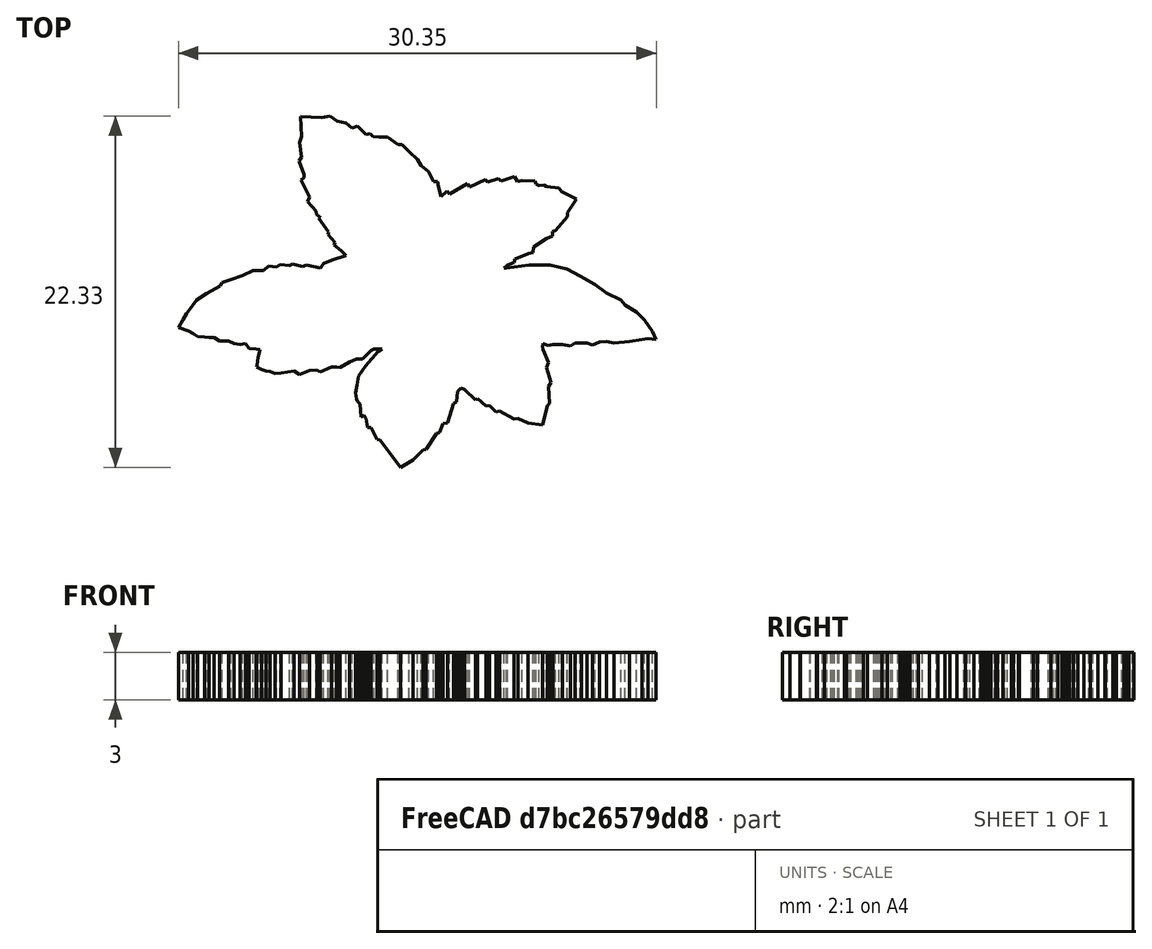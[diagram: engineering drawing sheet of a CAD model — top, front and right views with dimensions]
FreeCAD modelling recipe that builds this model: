
FCSTD DOCUMENT  (FreeCAD 0.20R29177 +233 (Git))
Label: mintsLeafLogo2022_10_12
License: All rights reserved
LicenseURL: http://en.wikipedia.org/wiki/All_rights_reserved
objects: Image::ImagePlane×1, Sketcher::SketchObject×1, PartDesign::Pad×1, PartDesign::Body×1
note: 4 computed .brp shape members not serialized (recipe doc carries the construction recipe); baked Part::Feature solids carry a one-line shape summary decoded from their .brp

FEATURE [Image::ImagePlane] ImagePlane
  XSize = 33.2103
  YSize = 25.9888
FEATURE [Sketcher::SketchObject] Sketch
  FullyConstrained = false
  MapMode = 5
  Support = -> [XY_Plane]
  sketch-geometry (205):
    g0: LineSegment StartX=-15.0667 StartY=-2.9879 StartZ=0 EndX=-14.4175 EndY=-3.20194 EndZ=0
    g1: LineSegment StartX=-14.1386 StartY=-3.3581 StartZ=0 EndX=-13.8673 EndY=-3.55064 EndZ=0
    g2: LineSegment StartX=-10.8098 StartY=-4.00788 StartZ=0 EndX=-10.5716 EndY=-4.29909 EndZ=0
    g3: LineSegment StartX=-10.5716 StartY=-4.29909 StartZ=0 EndX=-10.1338 EndY=-4.33136 EndZ=0
    g4: LineSegment StartX=-10.1338 StartY=-4.33136 StartZ=0 EndX=-9.89036 EndY=-4.3898 EndZ=0
    g5: LineSegment StartX=-9.51656 StartY=-5.73022 StartZ=0 EndX=-9.24931 EndY=-5.76229 EndZ=0
    g6: LineSegment StartX=-9.24931 StartY=-5.76229 StartZ=0 EndX=-8.92861 EndY=-5.90126 EndZ=0
    g7: LineSegment StartX=-8.92861 StartY=-5.90126 StartZ=0 EndX=-8.54378 EndY=-5.86384 EndZ=0
    g8: LineSegment StartX=-8.54378 StartY=-5.86384 StartZ=0 EndX=-7.71788 EndY=-5.75845 EndZ=0
    g9: LineSegment StartX=-7.71788 StartY=-5.75845 StartZ=0 EndX=-7.37291 EndY=-5.97257 EndZ=0
    g10: LineSegment StartX=-7.37291 StartY=-5.97257 StartZ=0 EndX=-6.72487 EndY=-5.72038 EndZ=0
    g11: LineSegment StartX=-6.72487 StartY=-5.72038 StartZ=0 EndX=-6.27066 EndY=-5.69481 EndZ=0
    g12: LineSegment StartX=-6.27066 StartY=-5.69481 StartZ=0 EndX=-6.06223 EndY=-5.80493 EndZ=0
    g13: LineSegment StartX=-6.06223 StartY=-5.80493 StartZ=0 EndX=-5.35089 EndY=-5.48914 EndZ=0
    g14: LineSegment StartX=-5.35089 StartY=-5.48914 StartZ=0 EndX=-5.02402 EndY=-5.48914 EndZ=0
    g15: LineSegment StartX=-5.02402 StartY=-5.48914 StartZ=0 EndX=-4.80126 EndY=-5.53132 EndZ=0
    g16: LineSegment StartX=-4.80126 StartY=-5.53132 StartZ=0 EndX=-4.19735 EndY=-5.16248 EndZ=0
    g17: LineSegment StartX=-3.75191 StartY=-4.97251 StartZ=0 EndX=-3.37714 EndY=-4.97251 EndZ=0
    g18: LineSegment StartX=-3.37714 StartY=-4.97251 StartZ=0 EndX=-2.81898 EndY=-4.45422 EndZ=0
    g19: LineSegment StartX=-2.81898 StartY=-4.45422 StartZ=0 EndX=-2.62761 EndY=-4.34259 EndZ=0
    g20: LineSegment StartX=-2.62761 StartY=-4.34259 StartZ=0 EndX=-2.15112 EndY=-4.35765 EndZ=0
    g21: LineSegment StartX=-2.38042 StartY=-4.51801 StartZ=0 EndX=-3.18577 EndY=-5.42702 EndZ=0
    g22: LineSegment StartX=-3.18577 StartY=-5.42702 StartZ=0 EndX=-3.61318 EndY=-6.05824 EndZ=0
    g23: LineSegment StartX=-3.61318 StartY=-6.05824 StartZ=0 EndX=-3.7111 EndY=-6.64579 EndZ=0
    g24: LineSegment StartX=-3.7111 StartY=-6.64579 StartZ=0 EndX=-3.83514 EndY=-7.15501 EndZ=0
    g25: LineSegment StartX=-3.83514 StartY=-7.15501 StartZ=0 EndX=-3.75878 EndY=-7.50876 EndZ=0
    g26: LineSegment StartX=-3.75878 StartY=-7.50876 StartZ=0 EndX=-3.70596 EndY=-7.68135 EndZ=0
    g27: LineSegment StartX=-3.70596 StartY=-7.68135 StartZ=0 EndX=-3.53967 EndY=-7.85202 EndZ=0
    g28: LineSegment StartX=-3.53967 StartY=-7.85202 StartZ=0 EndX=-3.4685 EndY=-8.65617 EndZ=0
    g29: LineSegment StartX=-3.27268 StartY=-8.56671 StartZ=0 EndX=-3.16823 EndY=-8.76909 EndZ=0
    g30: LineSegment StartX=-3.07088 StartY=-9.32083 StartZ=0 EndX=-2.84207 EndY=-9.3355 EndZ=0
    g31: LineSegment StartX=-2.84207 StartY=-9.3355 StartZ=0 EndX=-2.45193 EndY=-10.0982 EndZ=0
    g32: LineSegment StartX=-2.45193 StartY=-10.0982 StartZ=0 EndX=-2.24953 EndY=-10.1304 EndZ=0
    g33: LineSegment StartX=-2.24953 StartY=-10.1304 StartZ=0 EndX=-0.96042 EndY=-11.8753 EndZ=0
    g34: LineSegment StartX=-0.96042 StartY=-11.8753 StartZ=0 EndX=-0.153326 EndY=-11.3889 EndZ=0
    g35: LineSegment StartX=-0.153326 StartY=-11.3889 StartZ=0 EndX=0.461347 EndY=-10.7689 EndZ=0
    g36: LineSegment StartX=0.461347 StartY=-10.7689 StartZ=0 EndX=0.669802 EndY=-10.7261 EndZ=0
    g37: LineSegment StartX=0.669802 StartY=-10.7261 StartZ=0 EndX=1.31724 EndY=-9.70998 EndZ=0
    g38: LineSegment StartX=1.31724 StartY=-9.70998 StartZ=0 EndX=1.51826 EndY=-9.65081 EndZ=0
    g39: LineSegment StartX=1.51826 StartY=-9.65081 StartZ=0 EndX=1.74022 EndY=-9.08937 EndZ=0
    g40: LineSegment StartX=1.74022 StartY=-9.08937 StartZ=0 EndX=2.02094 EndY=-9.04367 EndZ=0
    g41: LineSegment StartX=2.02094 StartY=-9.04367 StartZ=0 EndX=2.39306 EndY=-7.80327 EndZ=0
    g42: LineSegment StartX=2.39306 StartY=-7.80327 StartZ=0 EndX=2.58839 EndY=-7.69871 EndZ=0
    g43: LineSegment StartX=2.6542 StartY=-7.03945 StartZ=0 EndX=2.86963 EndY=-6.81749 EndZ=0
    g44: LineSegment StartX=2.86963 StartY=-6.81749 StartZ=0 EndX=3.0916 EndY=-6.92847 EndZ=0
    g45: LineSegment StartX=3.0916 StartY=-6.92847 StartZ=0 EndX=3.79666 EndY=-7.57478 EndZ=0
    g46: LineSegment StartX=3.79666 StartY=-7.57478 StartZ=0 EndX=3.93376 EndY=-7.50297 EndZ=0
    g47: LineSegment StartX=3.93376 StartY=-7.50297 StartZ=0 EndX=4.46256 EndY=-7.97301 EndZ=0
    g48: LineSegment StartX=4.46256 StartY=-7.97301 StartZ=0 EndX=4.68452 EndY=-7.92079 EndZ=0
    g49: LineSegment StartX=4.68452 StartY=-7.92079 StartZ=0 EndX=5.1154 EndY=-8.34513 EndZ=0
    g50: LineSegment StartX=5.1154 StartY=-8.34513 StartZ=0 EndX=5.32431 EndY=-8.28637 EndZ=0
    g51: LineSegment StartX=5.32431 StartY=-8.28637 StartZ=0 EndX=6.23668 EndY=-8.79564 EndZ=0
    g52: LineSegment StartX=6.23668 StartY=-8.79564 StartZ=0 EndX=6.50362 EndY=-8.76631 EndZ=0
    g53: LineSegment StartX=6.50362 StartY=-8.76631 StartZ=0 EndX=7.14802 EndY=-9.05537 EndZ=0
    g54: LineSegment StartX=7.14802 StartY=-9.05537 StartZ=0 EndX=8.04883 EndY=-9.18613 EndZ=0
    g55: LineSegment StartX=8.04883 StartY=-9.18613 StartZ=0 EndX=8.36847 EndY=-7.93662 EndZ=0
    g56: LineSegment StartX=8.36847 StartY=-7.93662 StartZ=0 EndX=8.49923 EndY=-7.79133 EndZ=0
    g57: LineSegment StartX=8.49923 StartY=-7.79133 StartZ=0 EndX=8.43477 EndY=-6.72206 EndZ=0
    g58: LineSegment StartX=8.43477 StartY=-6.72206 StartZ=0 EndX=8.58621 EndY=-6.47988 EndZ=0
    g59: LineSegment StartX=8.58621 StartY=-6.47988 StartZ=0 EndX=8.32296 EndY=-5.53178 EndZ=0
    g60: LineSegment StartX=8.32296 StartY=-5.53178 StartZ=0 EndX=8.43984 EndY=-5.19091 EndZ=0
    g61: LineSegment StartX=8.43984 StartY=-5.19091 StartZ=0 EndX=8.07426 EndY=-4.39307 EndZ=0
    g62: LineSegment StartX=8.07426 StartY=-4.39307 StartZ=0 EndX=8.04236 EndY=-4.17777 EndZ=0
    g63: LineSegment StartX=8.04236 StartY=-4.17777 StartZ=0 EndX=8.0902 EndY=-3.99438 EndZ=0
    g64: LineSegment StartX=8.4103 StartY=-4.11103 StartZ=0 EndX=8.72013 EndY=-4.0502 EndZ=0
    g65: LineSegment StartX=8.72013 StartY=-4.0502 StartZ=0 EndX=9.31817 EndY=-4.0502 EndZ=0
    g66: LineSegment StartX=9.31817 StartY=-4.0502 StartZ=0 EndX=9.82964 EndY=-4.15887 EndZ=0
    g67: LineSegment StartX=10.1326 StartY=-3.9675 StartZ=0 EndX=10.5175 EndY=-3.9623 EndZ=0
    g68: LineSegment StartX=10.5175 StartY=-3.9623 StartZ=0 EndX=10.8831 EndY=-3.97536 EndZ=0
    g69: LineSegment StartX=10.8831 StartY=-3.97536 StartZ=0 EndX=11.2245 EndY=-4.09431 EndZ=0
    g70: LineSegment StartX=11.2245 StartY=-4.09431 StartZ=0 EndX=11.6861 EndY=-3.91007 EndZ=0
    g71: LineSegment StartX=11.6861 StartY=-3.91007 StartZ=0 EndX=12.1039 EndY=-3.88396 EndZ=0
    g72: LineSegment StartX=12.1039 StartY=-3.88396 StartZ=0 EndX=12.6 EndY=-3.9623 EndZ=0
    g73: LineSegment StartX=12.6 StartY=-3.9623 StartZ=0 EndX=13.5793 EndY=-3.87743 EndZ=0
    g74: LineSegment StartX=13.5793 StartY=-3.87743 StartZ=0 EndX=14.3888 EndY=-3.74687 EndZ=0
    g75: LineSegment StartX=14.3888 StartY=-3.74687 StartZ=0 EndX=14.7544 EndY=-3.68158 EndZ=0
    g76: LineSegment StartX=14.7544 StartY=-3.68158 StartZ=0 EndX=15.2767 EndY=-3.75339 EndZ=0
    g77: LineSegment StartX=15.2767 StartY=-3.75339 StartZ=0 EndX=15.0432 EndY=-3.24137 EndZ=0
    g78: LineSegment StartX=15.0432 StartY=-3.24137 StartZ=0 EndX=14.5209 EndY=-2.51672 EndZ=0
    g79: LineSegment StartX=14.5209 StartY=-2.51672 StartZ=0 EndX=14.0378 EndY=-1.99445 EndZ=0
    g80: LineSegment StartX=14.0378 StartY=-1.99445 StartZ=0 EndX=13.2802 EndY=-1.54625 EndZ=0
    g81: LineSegment StartX=13.2802 StartY=-1.54625 StartZ=0 EndX=13.0438 EndY=-1.23117 EndZ=0
    g82: LineSegment StartX=13.0438 StartY=-1.23117 StartZ=0 EndX=12.1074 EndY=-0.797939 EndZ=0
    g83: LineSegment StartX=12.1074 StartY=-0.797939 StartZ=0 EndX=11.3804 EndY=-0.250878 EndZ=0
    g84: LineSegment StartX=11.3804 StartY=-0.250878 StartZ=0 EndX=10.4396 EndY=0.304889 EndZ=0
    g85: LineSegment StartX=10.4396 StartY=0.304889 StartZ=0 EndX=9.59526 EndY=0.727998 EndZ=0
    g86: LineSegment StartX=9.59526 StartY=0.727998 StartZ=0 EndX=8.53624 EndY=0.97306 EndZ=0
    g87: LineSegment StartX=8.53624 StartY=0.97306 StartZ=0 EndX=7.199 EndY=0.97306 EndZ=0
    g88: LineSegment StartX=7.199 StartY=0.97306 StartZ=0 EndX=5.77932 EndY=0.795578 EndZ=0
    g89: LineSegment StartX=5.77932 StartY=0.795578 StartZ=0 EndX=5.60186 EndY=0.795578 EndZ=0
    g90: LineSegment StartX=5.60186 StartY=0.795578 StartZ=0 EndX=5.83178 EndY=0.981815 EndZ=0
    g91: LineSegment StartX=5.83178 StartY=0.981815 StartZ=0 EndX=6.25403 EndY=1.1582 EndZ=0
    g92: LineSegment StartX=6.30214 StartY=1.38269 StartZ=0 EndX=7.17987 EndY=1.70686 EndZ=0
    g93: LineSegment StartX=7.17987 StartY=1.70686 StartZ=0 EndX=7.44682 EndY=1.79438 EndZ=0
    g94: LineSegment StartX=7.44682 StartY=1.79438 StartZ=0 EndX=7.49058 EndY=2.12696 EndZ=0
    g95: LineSegment StartX=7.49058 StartY=2.12696 StartZ=0 EndX=8.30058 EndY=2.66839 EndZ=0
    g96: LineSegment StartX=8.30058 StartY=2.66839 StartZ=0 EndX=8.68575 EndY=2.81854 EndZ=0
    g97: LineSegment StartX=8.68575 StartY=2.81854 StartZ=0 EndX=8.68575 EndY=3.12537 EndZ=0
    g98: LineSegment StartX=8.68575 StartY=3.12537 StartZ=0 EndX=8.89508 EndY=3.18684 EndZ=0
    g99: LineSegment StartX=8.89508 StartY=3.18684 StartZ=0 EndX=9.63492 EndY=4.06602 EndZ=0
    g100: LineSegment StartX=9.63492 StartY=4.06602 StartZ=0 EndX=9.62638 EndY=4.32743 EndZ=0
    g101: LineSegment StartX=9.62638 StartY=4.32743 StartZ=0 EndX=10.2068 EndY=5.18314 EndZ=0
    g102: LineSegment StartX=10.2068 StartY=5.18314 StartZ=0 EndX=9.25518 EndY=5.64445 EndZ=0
    g103: LineSegment StartX=9.1102 StartY=5.87597 StartZ=0 EndX=8.32132 EndY=5.97336 EndZ=0
    g104: LineSegment StartX=8.32132 StartY=5.97336 StartZ=0 EndX=8.15466 EndY=6.06625 EndZ=0
    g105: LineSegment StartX=7.63471 StartY=6.13088 StartZ=0 EndX=7.56391 EndY=6.33267 EndZ=0
    g106: LineSegment StartX=7.56391 StartY=6.33267 StartZ=0 EndX=6.74832 EndY=6.35496 EndZ=0
    g107: LineSegment StartX=6.74832 StartY=6.35496 StartZ=0 EndX=6.46819 EndY=6.29526 EndZ=0
    g108: LineSegment StartX=6.46819 StartY=6.29526 StartZ=0 EndX=6.27042 EndY=6.61061 EndZ=0
    g109: LineSegment StartX=6.27042 StartY=6.61061 StartZ=0 EndX=5.40453 EndY=6.33267 EndZ=0
    g110: LineSegment StartX=5.40453 StartY=6.33267 StartZ=0 EndX=5.27091 EndY=6.47164 EndZ=0
    g111: LineSegment StartX=5.27091 StartY=6.47164 StartZ=0 EndX=4.56942 EndY=6.24725 EndZ=0
    g112: LineSegment StartX=4.56942 StartY=6.24725 StartZ=0 EndX=4.44161 EndY=6.40652 EndZ=0
    g113: LineSegment StartX=4.44161 StartY=6.40652 StartZ=0 EndX=3.4195 EndY=5.94588 EndZ=0
    g114: LineSegment StartX=3.4195 StartY=5.94588 StartZ=0 EndX=3.29192 EndY=6.1532 EndZ=0
    g115: LineSegment StartX=3.29192 StartY=6.1532 StartZ=0 EndX=2.15964 EndY=5.49137 EndZ=0
    g116: LineSegment StartX=2.15964 StartY=5.49137 StartZ=0 EndX=2.00016 EndY=5.69869 EndZ=0
    g117: LineSegment StartX=2.00016 StartY=5.69869 StartZ=0 EndX=1.6185 EndY=5.34828 EndZ=0
    g118: LineSegment StartX=1.6185 StartY=5.34828 StartZ=0 EndX=1.45984 EndY=5.94974 EndZ=0
    g119: LineSegment StartX=1.38165 StartY=6.28651 StartZ=0 EndX=1.14534 EndY=6.29963 EndZ=0
    g120: LineSegment StartX=0.348522 StartY=7.29544 StartZ=0 EndX=0.126706 EndY=7.68126 EndZ=0
    g121: LineSegment StartX=0.126706 StartY=7.68126 StartZ=0 EndX=-0.415308 EndY=8.18163 EndZ=0
    g122: LineSegment StartX=-0.415308 StartY=8.18163 StartZ=0 EndX=-0.872658 EndY=8.6237 EndZ=0
    g123: LineSegment StartX=-0.872658 StartY=8.6237 StartZ=0 EndX=-1.12074 EndY=8.64329 EndZ=0
    g124: LineSegment StartX=-1.12074 StartY=8.64329 StartZ=0 EndX=-1.79316 EndY=9.11986 EndZ=0
    g125: LineSegment StartX=-1.79316 StartY=9.11986 StartZ=0 EndX=-2.31488 EndY=9.12122 EndZ=0
    g126: LineSegment StartX=-2.31488 StartY=9.12122 StartZ=0 EndX=-2.71321 EndY=9.13846 EndZ=0
    g127: LineSegment StartX=-2.71321 StartY=9.13846 StartZ=0 EndX=-2.88425 EndY=9.34157 EndZ=0
    g128: LineSegment StartX=-2.88425 StartY=9.34157 StartZ=0 EndX=-3.16779 EndY=9.26454 EndZ=0
    g129: LineSegment StartX=-3.70739 StartY=9.82796 StartZ=0 EndX=-4.04915 EndY=9.7003 EndZ=0
    g130: LineSegment StartX=-4.04915 StartY=9.7003 StartZ=0 EndX=-4.42988 EndY=10.011 EndZ=0
    g131: LineSegment StartX=-5.98947 StartY=10.3656 StartZ=0 EndX=-7.32605 EndY=10.4108 EndZ=0
    g132: LineSegment StartX=-7.25254 StartY=9.13254 StartZ=0 EndX=-7.36878 EndY=8.7693 EndZ=0
    g133: LineSegment StartX=-7.36878 StartY=8.7693 StartZ=0 EndX=-7.2614 EndY=7.83762 EndZ=0
    g134: LineSegment StartX=-7.2614 StartY=7.83762 StartZ=0 EndX=-7.41112 EndY=7.6042 EndZ=0
    g135: LineSegment StartX=-7.41112 StartY=7.6042 StartZ=0 EndX=-7.09216 EndY=6.74302 EndZ=0
    g136: LineSegment StartX=-7.09216 StartY=6.74302 StartZ=0 EndX=-7.10014 EndY=6.55962 EndZ=0
    g137: LineSegment StartX=-7.10014 StartY=6.55962 StartZ=0 EndX=-7.29151 EndY=6.3842 EndZ=0
    g138: LineSegment StartX=-7.29151 StartY=6.3842 StartZ=0 EndX=-6.74132 EndY=5.29976 EndZ=0
    g139: LineSegment StartX=-6.74132 StartY=5.29976 StartZ=0 EndX=-6.87495 EndY=5.02732 EndZ=0
    g140: LineSegment StartX=-6.87495 StartY=5.02732 StartZ=0 EndX=-6.31586 EndY=4.42065 EndZ=0
    g141: LineSegment StartX=-6.31586 StartY=4.42065 StartZ=0 EndX=-6.30396 EndY=4.19463 EndZ=0
    g142: LineSegment StartX=-6.30396 StartY=4.19463 StartZ=0 EndX=-6.05415 EndY=4.0043 EndZ=0
    g143: LineSegment StartX=-6.05415 StartY=4.0043 StartZ=0 EndX=-6.18501 EndY=3.95672 EndZ=0
    g144: LineSegment StartX=-6.18501 StartY=3.95672 StartZ=0 EndX=-5.54265 EndY=3.07645 EndZ=0
    g145: LineSegment StartX=-5.54265 StartY=3.07645 StartZ=0 EndX=-5.57833 EndY=2.90991 EndZ=0
    g146: LineSegment StartX=-5.57833 StartY=2.90991 StartZ=0 EndX=-5.1263 EndY=2.41029 EndZ=0
    g147: LineSegment StartX=-5.1263 StartY=2.41029 StartZ=0 EndX=-5.18578 EndY=2.26755 EndZ=0
    g148: LineSegment StartX=-5.18578 StartY=2.26755 StartZ=0 EndX=-4.73375 EndY=1.89878 EndZ=0
    g149: LineSegment StartX=-4.73375 StartY=1.89878 StartZ=0 EndX=-4.42446 EndY=1.5895 EndZ=0
    g150: LineSegment StartX=-4.42446 StartY=1.5895 StartZ=0 EndX=-5.31663 EndY=1.29211 EndZ=0
    g151: LineSegment StartX=-5.31663 StartY=1.29211 StartZ=0 EndX=-5.84004 EndY=1.08988 EndZ=0
    g152: LineSegment StartX=-5.84004 StartY=1.08988 StartZ=0 EndX=-6.04226 EndY=0.792495 EndZ=0
    g153: LineSegment StartX=-6.04226 StartY=0.792495 StartZ=0 EndX=-6.94632 EndY=0.994719 EndZ=0
    g154: LineSegment StartX=-6.94632 StartY=0.994719 StartZ=0 EndX=-7.19613 EndY=0.887659 EndZ=0
    g155: LineSegment StartX=-7.19613 StartY=0.887659 StartZ=0 EndX=-7.8147 EndY=1.0423 EndZ=0
    g156: LineSegment StartX=-7.8147 StartY=1.0423 StartZ=0 EndX=-8.02502 EndY=0.969153 EndZ=0
    g157: LineSegment StartX=-8.02502 StartY=0.969153 StartZ=0 EndX=-8.60267 EndY=1.03042 EndZ=0
    g158: LineSegment StartX=-8.60267 StartY=1.03042 StartZ=0 EndX=-8.8346 EndY=0.872878 EndZ=0
    g159: LineSegment StartX=-8.8346 StartY=0.872878 StartZ=0 EndX=-9.33349 EndY=0.929767 EndZ=0
    g160: LineSegment StartX=-9.33349 StartY=0.929767 StartZ=0 EndX=-9.66169 EndY=0.649695 EndZ=0
    g161: LineSegment StartX=-9.66169 StartY=0.649695 StartZ=0 EndX=-10.3249 EndY=0.649695 EndZ=0
    g162: LineSegment StartX=-10.3249 StartY=0.649695 StartZ=0 EndX=-11.0107 EndY=0.32425 EndZ=0
    g163: LineSegment StartX=-11.0107 StartY=0.32425 StartZ=0 EndX=-11.7283 EndY=0.053139 EndZ=0
    g164: LineSegment StartX=-11.7283 StartY=0.053139 StartZ=0 EndX=-12.2971 EndY=-0.13161 EndZ=0
    g165: LineSegment StartX=-12.2971 StartY=-0.13161 StartZ=0 EndX=-12.4212 EndY=-0.347049 EndZ=0
    g166: LineSegment StartX=-12.4212 StartY=-0.347049 StartZ=0 EndX=-13.296 EndY=-0.817096 EndZ=0
    g167: LineSegment StartX=-13.296 StartY=-0.817096 StartZ=0 EndX=-13.9227 EndY=-1.24144 EndZ=0
    g168: LineSegment StartX=-13.9227 StartY=-1.24144 StartZ=0 EndX=-14.1708 EndY=-1.59398 EndZ=0
    g169: LineSegment StartX=-14.1708 StartY=-1.59398 StartZ=0 EndX=-14.5386 EndY=-2.09216 EndZ=0
    g170: LineSegment StartX=-14.5386 StartY=-2.09216 StartZ=0 EndX=-14.7831 EndY=-2.4577 EndZ=0
    g171: LineSegment StartX=-14.7831 StartY=-2.4577 StartZ=0 EndX=-15.0667 EndY=-2.9879 EndZ=0
    g172: LineSegment StartX=7.82861 StartY=6.04487 StartZ=0 EndX=7.63471 EndY=6.13088 EndZ=0
    g173: LineSegment StartX=-14.4175 StartY=-3.20194 StartZ=0 EndX=-14.1386 EndY=-3.3581 EndZ=0
    g174: LineSegment StartX=-13.8673 StartY=-3.55064 StartZ=0 EndX=-13.4107 EndY=-3.57136 EndZ=0
    g175: LineSegment StartX=-13.1321 StartY=-3.61699 StartZ=0 EndX=-12.817 EndY=-3.62343 EndZ=0
    g176: LineSegment StartX=-12.817 StartY=-3.62343 StartZ=0 EndX=-12.4662 EndY=-3.85302 EndZ=0
    g177: LineSegment StartX=-13.4107 StartY=-3.57136 StartZ=0 EndX=-13.1321 EndY=-3.61699 EndZ=0
    g178: LineSegment StartX=-12.4662 StartY=-3.85302 StartZ=0 EndX=-11.8704 EndY=-3.85302 EndZ=0
    g179: LineSegment StartX=-11.8704 StartY=-3.85302 StartZ=0 EndX=-11.5204 EndY=-4.00836 EndZ=0
    g180: LineSegment StartX=-11.5204 StartY=-4.00836 StartZ=0 EndX=-11.1389 EndY=-4.05555 EndZ=0
    g181: LineSegment StartX=-11.1389 StartY=-4.05555 StartZ=0 EndX=-10.8098 EndY=-4.00788 EndZ=0
    g182: LineSegment StartX=-9.89036 StartY=-4.3898 StartZ=0 EndX=-9.99555 EndY=-4.87697 EndZ=0
    g183: LineSegment StartX=-9.99555 StartY=-4.87697 StartZ=0 EndX=-10.0894 EndY=-5.36391 EndZ=0
    g184: LineSegment StartX=-10.0894 StartY=-5.36391 StartZ=0 EndX=-10.107 EndY=-5.50471 EndZ=0
    g185: LineSegment StartX=-10.107 StartY=-5.50471 StartZ=0 EndX=-9.77848 EndY=-5.63965 EndZ=0
    g186: LineSegment StartX=-9.77848 StartY=-5.63965 StartZ=0 EndX=-9.51656 EndY=-5.73022 EndZ=0
    g187: LineSegment StartX=-4.19735 StartY=-5.16248 StartZ=0 EndX=-3.75191 EndY=-4.97251 EndZ=0
    g188: LineSegment StartX=-2.38042 StartY=-4.51801 StartZ=0 EndX=-2.15112 EndY=-4.35765 EndZ=0
    g189: LineSegment StartX=-3.4685 StartY=-8.65617 StartZ=0 EndX=-3.27268 EndY=-8.56671 EndZ=0
    g190: LineSegment StartX=-3.16823 StartY=-8.76909 StartZ=0 EndX=-3.07088 EndY=-9.32083 EndZ=0
    g191: LineSegment StartX=2.58839 StartY=-7.69871 StartZ=0 EndX=2.6542 EndY=-7.03945 EndZ=0
    g192: LineSegment StartX=8.0902 StartY=-3.99438 StartZ=0 EndX=8.4103 EndY=-4.11103 EndZ=0
    g193: LineSegment StartX=9.82964 StartY=-4.15887 StartZ=0 EndX=10.1326 EndY=-3.9675 EndZ=0
    g194: LineSegment StartX=6.30214 StartY=1.38269 StartZ=0 EndX=6.25403 EndY=1.1582 EndZ=0
    g195: LineSegment StartX=1.38165 StartY=6.28651 StartZ=0 EndX=1.45984 EndY=5.94974 EndZ=0
    g196: LineSegment StartX=0.348522 StartY=7.29544 StartZ=0 EndX=0.824344 EndY=6.91479 EndZ=0
    g197: LineSegment StartX=0.824344 StartY=6.91479 StartZ=0 EndX=1.14534 EndY=6.29963 EndZ=0
    g198: LineSegment StartX=-3.70739 StartY=9.82796 StartZ=0 EndX=-3.16779 EndY=9.26454 EndZ=0
    g199: LineSegment StartX=-5.98947 StartY=10.3656 StartZ=0 EndX=-5.43038 EndY=10.4489 EndZ=0
    g200: LineSegment StartX=-5.43038 StartY=10.4489 StartZ=0 EndX=-4.9791 EndY=10.1425 EndZ=0
    g201: LineSegment StartX=-4.42988 StartY=10.011 StartZ=0 EndX=-4.9791 EndY=10.1425 EndZ=0
    g202: LineSegment StartX=-7.25254 StartY=9.13254 StartZ=0 EndX=-7.32605 EndY=10.4108 EndZ=0
    g203: LineSegment StartX=7.82861 StartY=6.04487 StartZ=0 EndX=8.15466 EndY=6.06625 EndZ=0
    g204: LineSegment StartX=9.1102 StartY=5.87597 StartZ=0 EndX=9.25518 EndY=5.64445 EndZ=0
  constraints (114):
    c: Coincident(g4,g3)
    c: Coincident(g6,g5)
    c: Coincident(g8,g7)
    c: Coincident(g9,g8)
    c: Coincident(g10,g9)
    c: Coincident(g11,g10)
    c: Coincident(g13,g12)
    c: Coincident(g16,g15)
    c: Coincident(g22,g21)
    c: Coincident(g25,g24)
    c: Coincident(g26,g25)
    c: Coincident(g28,g27)
    c: Coincident(g33,g32)
    c: Coincident(g37,g36)
    c: Coincident(g38,g37)
    c: Coincident(g40,g39)
    c: Coincident(g44,g43)
    c: Coincident(g51,g50)
    c: Coincident(g52,g51)
    c: Coincident(g57,g56)
    c: Coincident(g58,g57)
    c: Coincident(g59,g58)
    c: Coincident(g61,g60)
    c: Coincident(g63,g62)
    c: Coincident(g66,g65)
    c: Coincident(g70,g69)
    c: Coincident(g72,g71)
    c: Coincident(g73,g72)
    c: Coincident(g74,g73)
    c: Coincident(g77,g76)
    c: Coincident(g80,g79)
    c: Coincident(g81,g80)
    c: Coincident(g83,g82)
    c: Coincident(g85,g84)
    c: Coincident(g86,g85)
    c: Coincident(g87,g86)
    c: Coincident(g89,g88)
    c: Coincident(g90,g89)
    c: Coincident(g91,g90)
    c: Coincident(g93,g92)
    c: Coincident(g95,g94)
    c: Coincident(g97,g96)
    c: Coincident(g98,g97)
    c: Coincident(g99,g98)
    c: Coincident(g100,g99)
    c: Coincident(g104,g103)
    c: Coincident(g106,g105)
    c: Coincident(g107,g106)
    c: Coincident(g111,g110)
    c: Coincident(g113,g112)
    c: Coincident(g118,g117)
    c: Coincident(g122,g121)
    c: Coincident(g126,g125)
    c: Coincident(g130,g129)
    c: Coincident(g133,g132)
    c: Coincident(g134,g133)
    c: Coincident(g135,g134)
    c: Coincident(g139,g138)
    c: Coincident(g142,g141)
    c: Coincident(g156,g155)
    c: Coincident(g157,g156)
    c: Coincident(g159,g158)
    c: Coincident(g161,g160)
    c: Coincident(g164,g163)
    c: Coincident(g165,g164)
    c: Coincident(g168,g167)
    c: Coincident(g169,g168)
    c: Coincident(g171,g170)
    c: Coincident(g171,g0)
    c: Coincident(g172,g105)
    c: DistanceX(g165) = -12.4212
    c: DistanceY(g165) = -0.347049
    c: Coincident(g173,g0)
    c: Coincident(g173,g1)
    c: Coincident(g174,g1)
    c: Coincident(g177,g174)
    c: Coincident(g177,g175)
    c: Coincident(g178,g176)
    c: Coincident(g181,g2)
    c: Coincident(g182,g4)
    c: Coincident(g186,g185)
    c: Coincident(g186,g5)
    c: Coincident(g187,g16)
    c: Coincident(g187,g17)
    c: Coincident(g188,g21)
    c: Coincident(g188,g20)
    c: Coincident(g189,g28)
    c: Coincident(g189,g29)
    c: Coincident(g190,g29)
    c: Coincident(g190,g30)
    c: Coincident(g191,g42)
    c: Coincident(g191,g43)
    c: Coincident(g192,g63)
    c: Coincident(g192,g64)
    c: Coincident(g193,g66)
    c: Coincident(g193,g67)
    c: Coincident(g194,g92)
    c: Coincident(g194,g91)
    c: Coincident(g195,g119)
    c: Coincident(g195,g118)
    c: Coincident(g196,g120)
    c: Coincident(g197,g119)
    c: Coincident(g198,g129)
    c: Coincident(g198,g128)
    c: Coincident(g199,g131)
    c: Coincident(g200,g199)
    c: Coincident(g201,g130)
    c: Coincident(g201,g200)
    c: Coincident(g202,g132)
    c: Coincident(g202,g131)
    c: Coincident(g203,g172)
    c: Coincident(g203,g104)
    c: Coincident(g204,g103)
    c: Coincident(g204,g102)
FEATURE [PartDesign::Pad] Pad
  Direction = (0,0,1)
  Length = 3
  Length2 = 10
  Profile = -> Sketch
  ReferenceAxis = -> Sketch [N_Axis]
  Type = 0
FEATURE [PartDesign::Body] Body  label="logo"
  Group = -> [Sketch,Pad]
  Origin = -> Origin
  Tip = -> Pad
